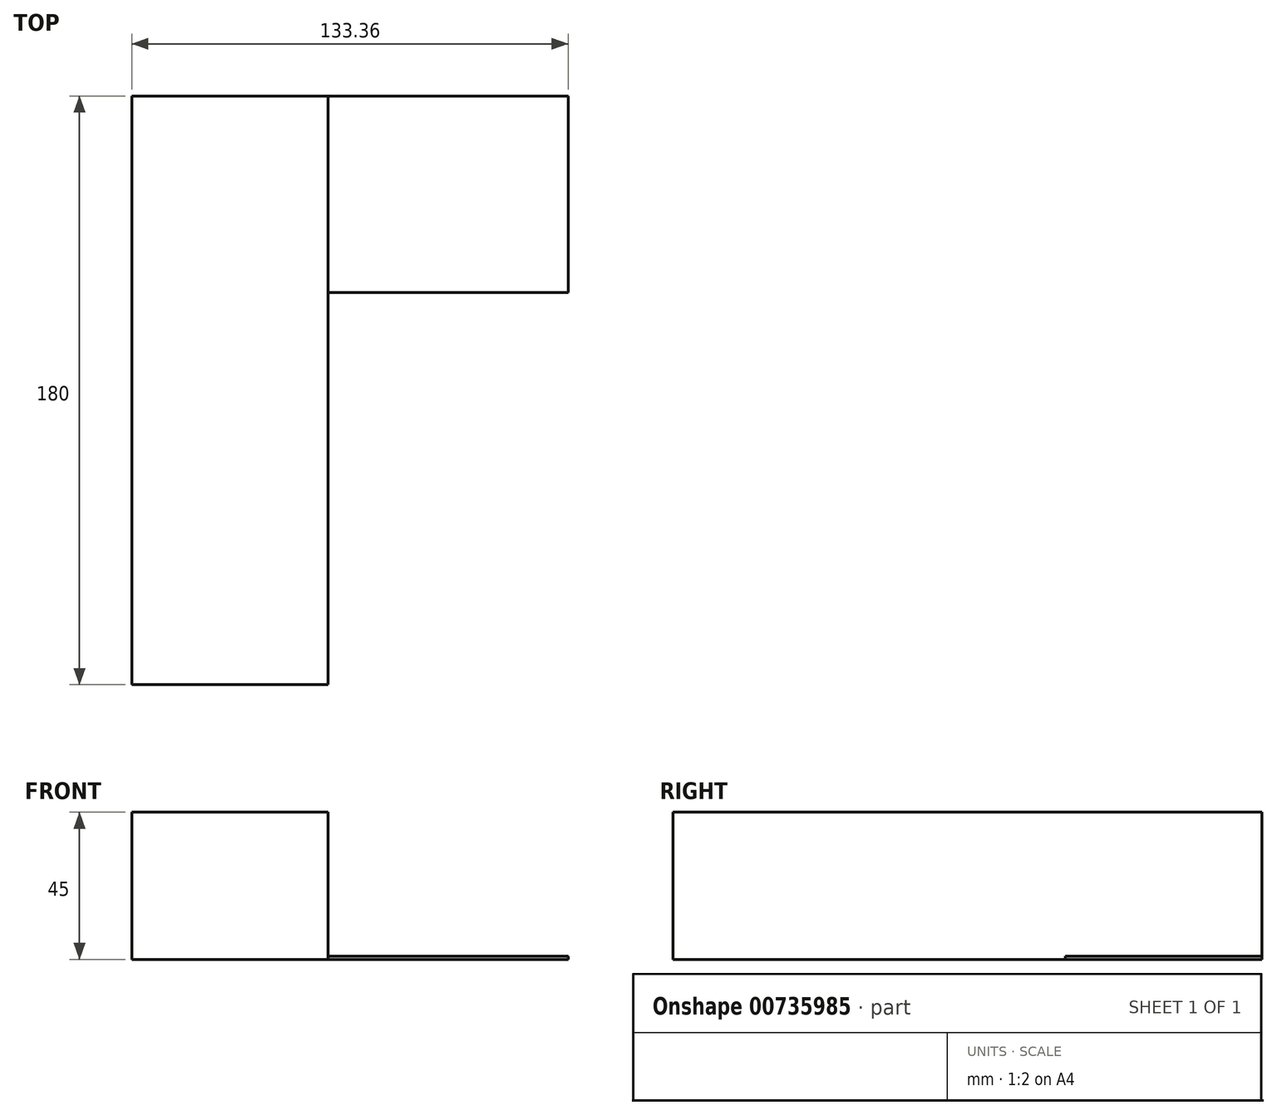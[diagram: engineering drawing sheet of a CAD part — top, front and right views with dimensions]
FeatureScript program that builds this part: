
annotation { "Feature Type Name" : "Feature", "Feature Type Description" : "" }
export const myFeature = defineFeature(function(context is Context, id is Id, definition is map)
    precondition{}
    {
        {
            var Q0;
            Q0=qCreatedBy(makeId("Top.planeOp"),FACE);
            var sketch = newSketch(context, id + "F0", { "sketchPlane" : qUnion([Q0])});
            skLineSegment(sketch, "E0.bottom", {"start": v(-147.27, 82.74) * mm, "end": v(-87.27, 82.74) * mm});
            skLineSegment(sketch, "E0.top", {"start": v(-147.27, -97.26) * mm, "end": v(-87.27, -97.26) * mm});
            skLineSegment(sketch, "E0.left", {"start": v(-147.27, 82.74) * mm, "end": v(-147.27, -97.26) * mm});
            skLineSegment(sketch, "E0.right", {"start": v(-87.27, 82.74) * mm, "end": v(-87.27, -97.26) * mm});
            skLineSegment(sketch, "E1.bottom", {"start": v(-87.27, 82.74) * mm, "end": v(-13.9, 82.74) * mm});
            skLineSegment(sketch, "E1.top", {"start": v(-87.27, 22.68) * mm, "end": v(-13.9, 22.68) * mm});
            skLineSegment(sketch, "E1.left", {"start": v(-87.27, 82.74) * mm, "end": v(-87.27, 22.68) * mm});
            skLineSegment(sketch, "E1.right", {"start": v(-13.9, 82.74) * mm, "end": v(-13.9, 22.68) * mm});
            skLineSegment(sketch, "E2.bottom", {"start": v(-87.27, 22.68) * mm, "end": v(-87.27, 22.68) * mm});
            skLineSegment(sketch, "E2.top", {"start": v(-87.27, -97.26) * mm, "end": v(-87.27, -97.26) * mm});
            skLineSegment(sketch, "E2.left", {"start": v(-87.27, 22.68) * mm, "end": v(-87.27, -97.26) * mm});
            skLineSegment(sketch, "E2.right", {"start": v(-87.27, 22.68) * mm, "end": v(-87.27, -97.26) * mm});
            skLineSegment(sketch, "E3.bottom", {"start": v(-67.27, -97.26) * mm, "end": v(-87.27, -97.26) * mm});
            skLineSegment(sketch, "E3.top", {"start": v(-67.27, 22.68) * mm, "end": v(-87.27, 22.68) * mm});
            skLineSegment(sketch, "E3.left", {"start": v(-67.27, -97.26) * mm, "end": v(-67.27, 22.68) * mm});
            skLineSegment(sketch, "E3.right", {"start": v(-87.27, -97.26) * mm, "end": v(-87.27, 22.68) * mm});
            skLineSegment(sketch, "E4.bottom", {"start": v(-67.27, 22.68) * mm, "end": v(-29.07, 22.68) * mm});
            skLineSegment(sketch, "E4.top", {"start": v(-67.27, -187.9) * mm, "end": v(-29.07, -187.9) * mm});
            skLineSegment(sketch, "E4.left", {"start": v(-67.27, 22.68) * mm, "end": v(-67.27, -187.9) * mm});
            skLineSegment(sketch, "E4.right", {"start": v(-29.07, 22.68) * mm, "end": v(-29.07, -187.9) * mm});
            skLineSegment(sketch, "E5", {"start": v(-50.59, 22.68) * mm, "end": v(-50.59, -187.9) * mm});
            skSolve(sketch);
        }
        {
            var Q0;
            {var subQ3=sQuery(id+"F0.wireOp",EDGE,"E0.bottom");Q0=makeQuery(id+"F0.imprint","IMPRINT",FACE,{"disambiguationData":[TD([[makeQuery(id+"F0.imprint","IMPRINT",EDGE,{"derivedFrom":subQ3}),-1.0]])]});}
            extrude(context, id + "F1", {"entities" : qUnion([Q0]), "depth" : 45 * mm, "offsetDistance" : 25 * mm});
        }
        {
            var Q0;
            {var subQ6=sQuery(id+"F0.wireOp",EDGE,"E1.bottom");Q0=makeQuery(id+"F0.imprint","IMPRINT",FACE,{"disambiguationData":[TD([[makeQuery(id+"F0.imprint","IMPRINT",EDGE,{"derivedFrom":subQ6}),-1.0]])]});}
            extrude(context, id + "F2", {"entities" : qUnion([Q0]), "operationType" : NewBodyOperationType.ADD, "depth" : 1 * mm, "offsetDistance" : 25 * mm});
        }
    });
